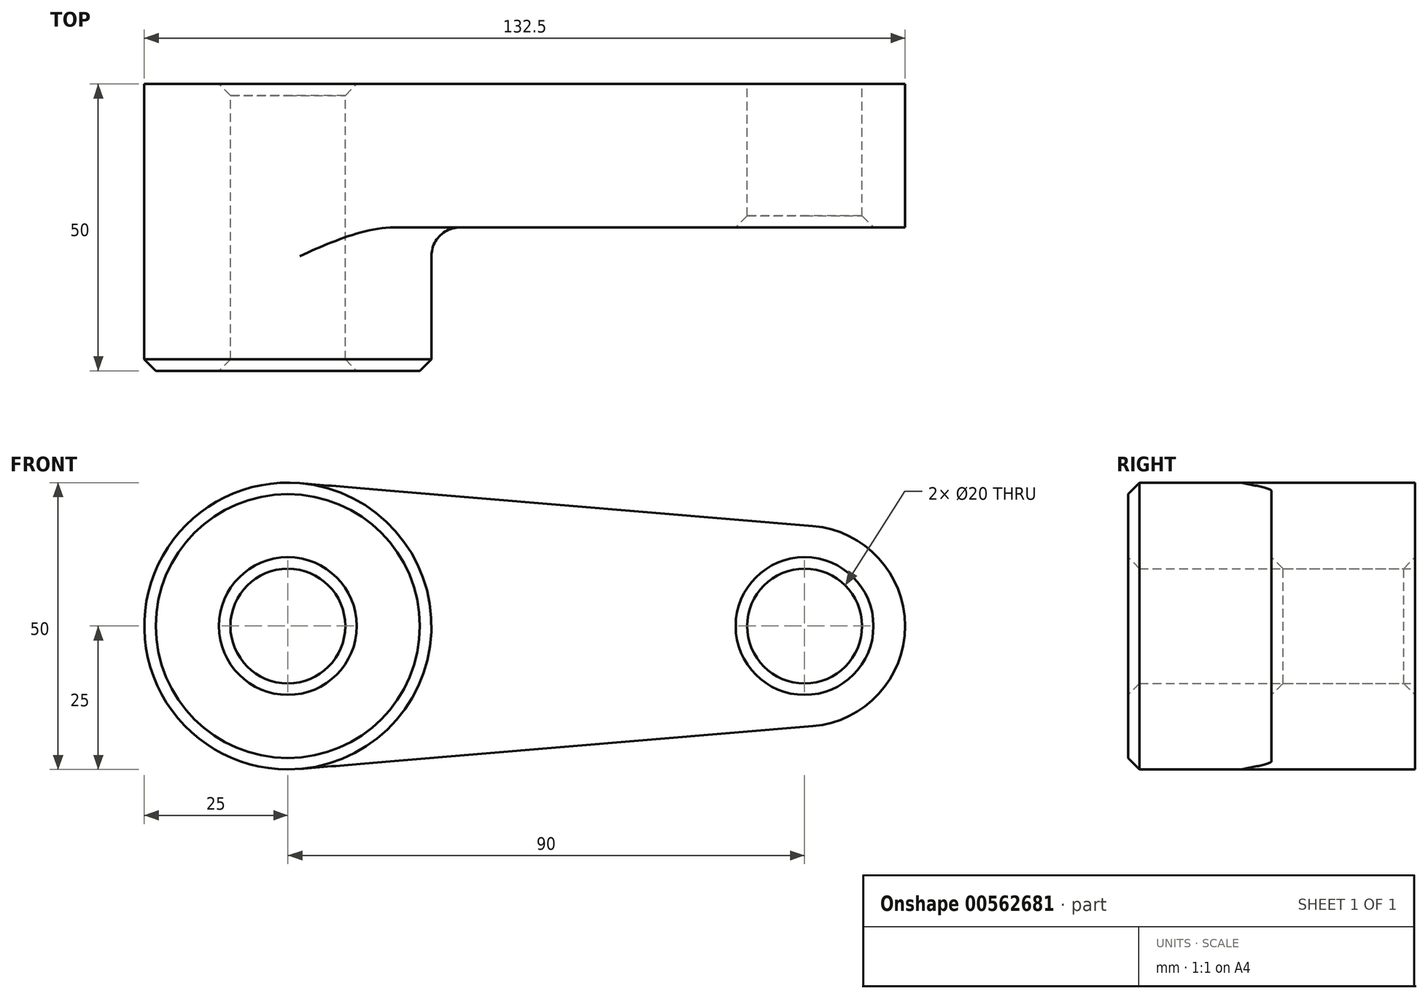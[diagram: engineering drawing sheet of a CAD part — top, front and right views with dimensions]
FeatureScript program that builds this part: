
annotation { "Feature Type Name" : "Feature", "Feature Type Description" : "" }
export const myFeature = defineFeature(function(context is Context, id is Id, definition is map)
    precondition{}
    {
        {
            var Q0;
            Q0=qCreatedBy(makeId("Front.planeOp"),FACE);
            var sketch = newSketch(context, id + "F0", { "sketchPlane" : qUnion([Q0])});
            skCircle(sketch, "E0", {"center": v(0, 0) * mm, "radius": 25 * mm});
            skCircle(sketch, "E1", {"center": v(90, 0) * mm, "radius": 17.5 * mm});
            skLineSegment(sketch, "E2", {"start": v(2.08, 24.91) * mm, "end": v(91.46, 17.44) * mm});
            skLineSegment(sketch, "E3", {"start": v(2.08, -24.91) * mm, "end": v(91.46, -17.44) * mm});
            skCircle(sketch, "E4", {"center": v(0, 0) * mm, "radius": 10 * mm});
            skCircle(sketch, "E5", {"center": v(90, 0) * mm, "radius": 10 * mm});
            skSolve(sketch);
        }
        {
            var Q0;
            Q0 = qSketchRegion(id + "F0", true);
            extrude(context, id + "F1", {"entities" : qUnion([Q0]), "depth" : 25 * mm, "offsetDistance" : 25 * mm});
        }
        {
            var Q0;
            Q0=makeQuery(id+"F0.imprint","IMPRINT",FACE,{"disambiguationData":[TD([[makeQuery(id+"F0.imprint","IMPRINT",EDGE,{"derivedFrom":sQuery(id+"F0.wireOp",EDGE,"E4")}),-1.0]])]});
            extrude(context, id + "F2", {"entities" : qUnion([Q0]), "operationType" : NewBodyOperationType.ADD, "depth" : 50 * mm, "offsetDistance" : 25 * mm});
        }
        {
            var Q0;
            {var subQ0=sQuery(id+"F0.wireOp",EDGE,"E0");Q0=makeQuery(id+"F2.boolean.opBoolean","INTERSECT",EDGE,{"derivedFrom":[makeQuery(id+"F1.opExtrude","CAP_FACE",FACE,{"disambiguationData":[OSD([subQ0,sQuery(id+"F0.wireOp",EDGE,"E1"),sQuery(id+"F0.wireOp",EDGE,"E2"),sQuery(id+"F0.wireOp",EDGE,"E3"),sQuery(id+"F0.wireOp",EDGE,"E4"),sQuery(id+"F0.wireOp",EDGE,"E5")])],"isStart":false}),makeQuery(id+"F2.opExtrude","SWEPT_FACE",FACE,{"disambiguationData":[OSD([subQ0])]})]});}
            fillet(context, id + "F3", {"entities" : qUnion([Q0]), "radius" : 5 * mm, "tangentPropagation" : true, "allowEdgeOverflow" : false});
        }
        {
            var Q0;
            {var subQ0=sQuery(id+"F0.wireOp",EDGE,"E4");Q0=makeQuery(id+"F2.boolean.opBoolean","MERGE",FACE,{"derivedFrom":[makeQuery(id+"F1.opExtrude","SWEPT_FACE",FACE,{"disambiguationData":[OSD([subQ0])]}),makeQuery(id+"F2.opExtrude","SWEPT_FACE",FACE,{"disambiguationData":[OSD([subQ0])]})]});}
            var Q1;
            Q1=makeQuery(id+"F2.opExtrude","CAP_EDGE",EDGE,{"disambiguationData":[OSD([sQuery(id+"F0.wireOp",EDGE,"E0")])],"isStart":false});
            var Q2;
            Q2=makeQuery(id+"F1.opExtrude","CAP_EDGE",EDGE,{"disambiguationData":[OSD([sQuery(id+"F0.wireOp",EDGE,"E5")])],"isStart":false});
            chamfer(context, id + "F4", {"entities" : qUnion([Q0, Q1, Q2]), "width" : 2 * mm, "tangentPropagation" : true});
        }
    });
